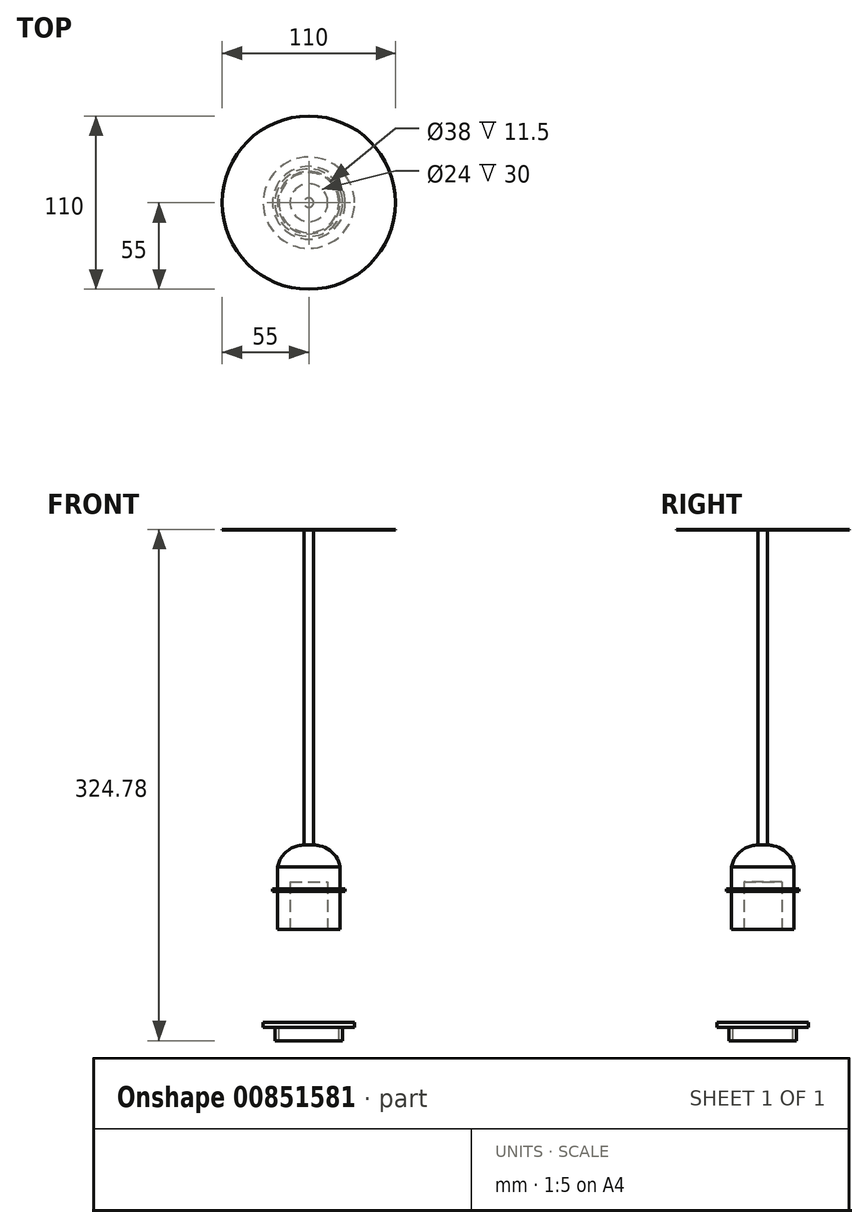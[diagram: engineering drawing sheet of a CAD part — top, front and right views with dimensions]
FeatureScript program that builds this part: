
annotation { "Feature Type Name" : "Feature", "Feature Type Description" : "" }
export const myFeature = defineFeature(function(context is Context, id is Id, definition is map)
    precondition{}
    {
        {
            var Q0;
            Q0=qCreatedBy(makeId("Front.planeOp"),FACE);
            var sketch = newSketch(context, id + "F0", { "sketchPlane" : qUnion([Q0])});
            skLineSegment(sketch, "E0", {"start": v(0, 58.84) * mm, "end": v(12, 58.84) * mm});
            skLineSegment(sketch, "E1", {"start": v(12, 58.84) * mm, "end": v(12, 28.84) * mm});
            skLineSegment(sketch, "E2", {"start": v(12, 28.84) * mm, "end": v(19.85, 28.84) * mm});
            skLineSegment(sketch, "E3", {"start": v(19.85, 28.84) * mm, "end": v(19.85, 52.84) * mm});
            skLineSegment(sketch, "E4", {"start": v(19.85, 52.84) * mm, "end": v(23.1, 52.84) * mm});
            skLineSegment(sketch, "E5", {"start": v(23.1, 52.84) * mm, "end": v(23.1, 54.34) * mm});
            skLineSegment(sketch, "E6", {"start": v(0, 12.12) * mm, "end": v(0, 28.84) * mm, "construction": true});
            skLineSegment(sketch, "E7", {"start": v(3, 82.34) * mm, "end": v(3, 282.34) * mm});
            skLineSegment(sketch, "E8", {"start": v(3, 282.34) * mm, "end": v(55, 282.34) * mm});
            skLineSegment(sketch, "E9", {"start": v(55, 282.86) * mm, "end": v(0, 282.86) * mm});
            skLineSegment(sketch, "E10", {"start": v(0, 282.86) * mm, "end": v(0, 58.84) * mm});
            skArc(sketch, "E11.filletArc", {"start": v(19.85, 68.34) * mm, "mid": v(13.98, 78.42) * mm, "end": v(3, 82.34) * mm});
            skLineSegment(sketch, "E12", {"start": v(23.1, 54.34) * mm, "end": v(19.85, 54.34) * mm});
            skLineSegment(sketch, "E13", {"start": v(19.85, 54.34) * mm, "end": v(19.85, 68.34) * mm});
            skLineSegment(sketch, "E14", {"start": v(55, 282.86) * mm, "end": v(55, 282.34) * mm});
            skSolve(sketch);
        }
        {
            var Q0;
            Q0 = qSketchRegion(id + "F0", true);
            var Q1;
            Q1=sQuery(id+"F0.wireOp",EDGE,"E6");
            revolve(context, id + "F1", {"surfaceOperationType" : NewSurfaceOperationType.NEW, "entities" : qUnion([Q0]), "axis" : qUnion([Q1]), "revolveType" : RevolveType.FULL});
        }
        {
            var Q0;
            Q0=qCreatedBy(makeId("Front.planeOp"),FACE);
            var sketch = newSketch(context, id + "F2", { "sketchPlane" : qUnion([Q0])});
            skLineSegment(sketch, "E15", {"start": v(0, -30.42) * mm, "end": v(0, -44.95) * mm, "construction": true});
            skLineSegment(sketch, "E16.MirrorCS", {"start": v(29, -33.42) * mm, "end": v(29, -30.42) * mm});
            skLineSegment(sketch, "E17.MirrorCS", {"start": v(19, -41.92) * mm, "end": v(21.5, -41.92) * mm});
            skLineSegment(sketch, "E18.MirrorCS", {"start": v(21.5, -33.42) * mm, "end": v(29, -33.42) * mm});
            skLineSegment(sketch, "E19.MirrorCS", {"start": v(19, -30.42) * mm, "end": v(19, -41.92) * mm});
            skLineSegment(sketch, "E20.MirrorCS", {"start": v(21.5, -41.92) * mm, "end": v(21.5, -33.42) * mm});
            skLineSegment(sketch, "E21.MirrorCS", {"start": v(29, -30.42) * mm, "end": v(19, -30.42) * mm});
            skSolve(sketch);
        }
        {
            var Q0;
            Q0 = qSketchRegion(id + "F2", true);
            var Q1;
            Q1=sQuery(id+"F2.wireOp",EDGE,"E15");
            revolve(context, id + "F3", {"surfaceOperationType" : NewSurfaceOperationType.NEW, "entities" : qUnion([Q0]), "axis" : qUnion([Q1]), "revolveType" : RevolveType.FULL});
        }
    });
